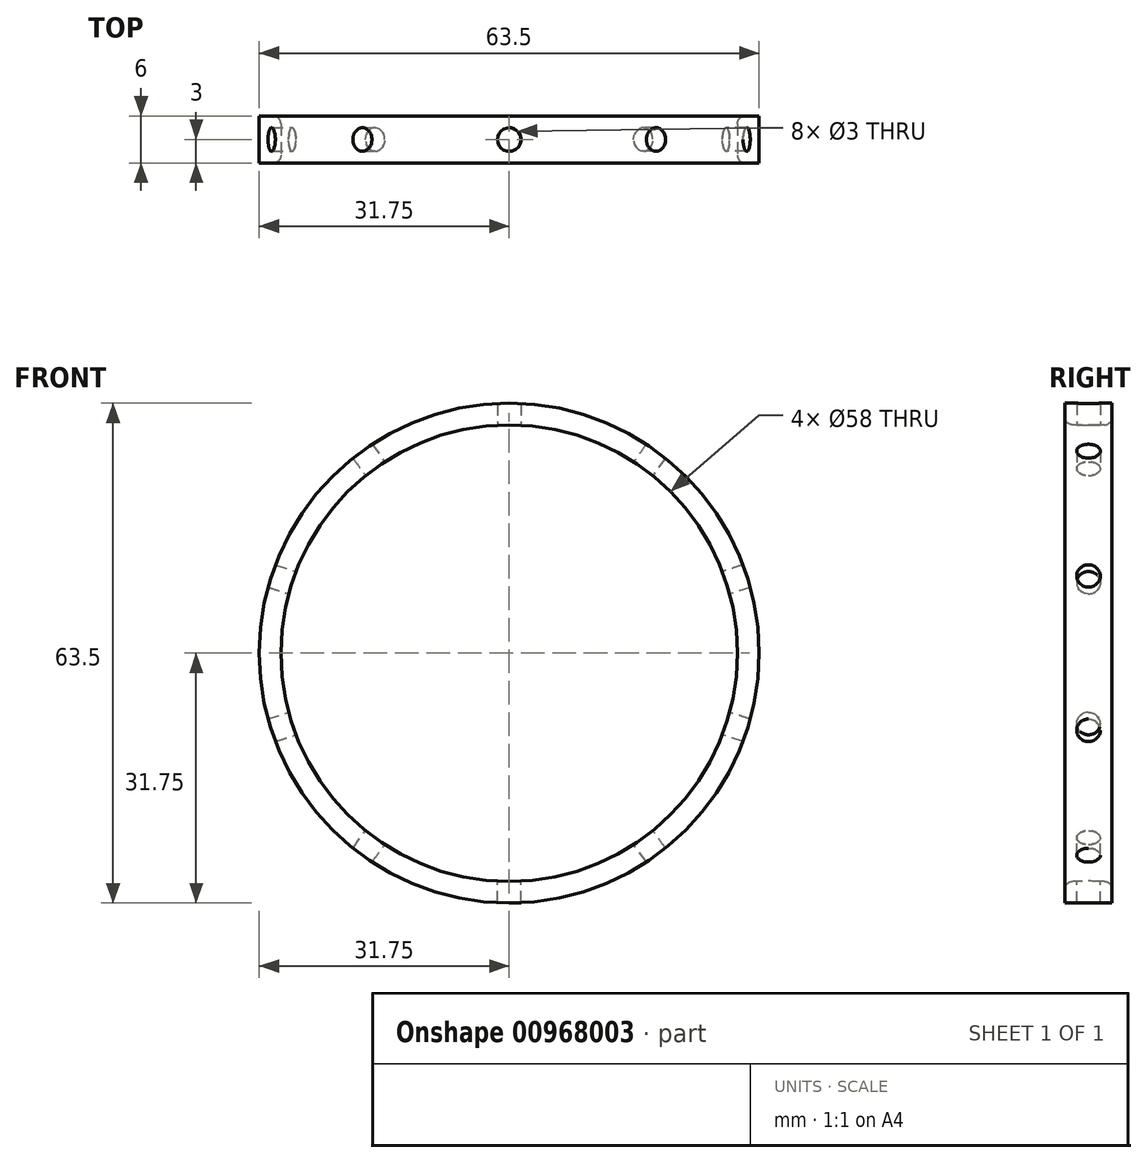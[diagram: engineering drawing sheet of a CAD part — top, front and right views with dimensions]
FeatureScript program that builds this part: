
annotation { "Feature Type Name" : "Feature", "Feature Type Description" : "" }
export const myFeature = defineFeature(function(context is Context, id is Id, definition is map)
    precondition{}
    {
        {
            var Q0;
            Q0=qCreatedBy(makeId("Front.planeOp"),FACE);
            var sketch = newSketch(context, id + "F0", { "sketchPlane" : qUnion([Q0])});
            skCircle(sketch, "E0", {"center": v(0, 0) * mm, "radius": 29 * mm});
            skCircle(sketch, "E1", {"center": v(0, 0) * mm, "radius": 31.75 * mm});
            skSolve(sketch);
        }
        {
            var Q0;
            Q0=makeQuery(id+"F0.imprint","IMPRINT",FACE,{"disambiguationData":[TD([[makeQuery(id+"F0.imprint","IMPRINT",EDGE,{"derivedFrom":sQuery(id+"F0.wireOp",EDGE,"E0")}),-1.0]])]});
            extrude(context, id + "F1", {"entities" : qUnion([Q0]), "endBound" : BoundingType.SYMMETRIC, "oppositeDirection" : true, "depth" : 6 * mm, "offsetDistance" : 25 * mm});
        }
        {
            var Q0;
            Q0=makeQuery(id+"F1.opExtrude","CAP_EDGE",EDGE,{"disambiguationData":[OSD([sQuery(id+"F0.wireOp",EDGE,"E0")])],"isStart":true});
            var Q1;
            Q1=makeQuery(id+"F1.opExtrude","CAP_EDGE",EDGE,{"disambiguationData":[OSD([sQuery(id+"F0.wireOp",EDGE,"E0")])],"isStart":false});
            fillet(context, id + "F2", {"entities" : qUnion([Q0, Q1]), "radius" : 1 * mm, "tangentPropagation" : true, "allowEdgeOverflow" : false});
        }
        {
            var Q0;
            Q0=qCreatedBy(makeId("Top.planeOp"),FACE);
            var sketch = newSketch(context, id + "F3", { "sketchPlane" : qUnion([Q0])});
            skCircle(sketch, "E2", {"center": v(0, 0) * mm, "radius": 1.5 * mm});
            skSolve(sketch);
        }
        {
            var Q0;
            Q0 = qSketchRegion(id + "F3", true);
            extrude(context, id + "F4", {"entities" : qUnion([Q0]), "depth" : 40 * mm, "offsetDistance" : 25 * mm, "hasSecondDirection" : true, "secondDirectionOppositeDirection" : false, "secondDirectionDepth" : 25 * mm});
        }
        {
            var Q0;
            Q0=qCreatedBy(makeId("Top.planeOp"),FACE);
            var sketch = newSketch(context, id + "F5", { "sketchPlane" : qUnion([Q0])});
            skLineSegment(sketch, "E3", {"start": v(0, 0) * mm, "end": v(0, 14.55) * mm});
            skSolve(sketch);
        }
        {
            var Q0;
            Q0=makeQuery(id+"F4.opExtrude","SWEPT_BODY",BODY,{"disambiguationData":[OSD([sQuery(id+"F3.wireOp",EDGE,"E2")])]});
            var Q1;
            Q1=sQuery(id+"F5.wireOp",EDGE,"E3");
            circularPattern(context, id + "F6", {"operationType" : NewBodyOperationType.REMOVE, "entities" : qUnion([Q0]), "axis" : qUnion([Q1]), "angle" : 360 * degree, "instanceCount" : 10, "equalSpace" : true});
        }
    });
